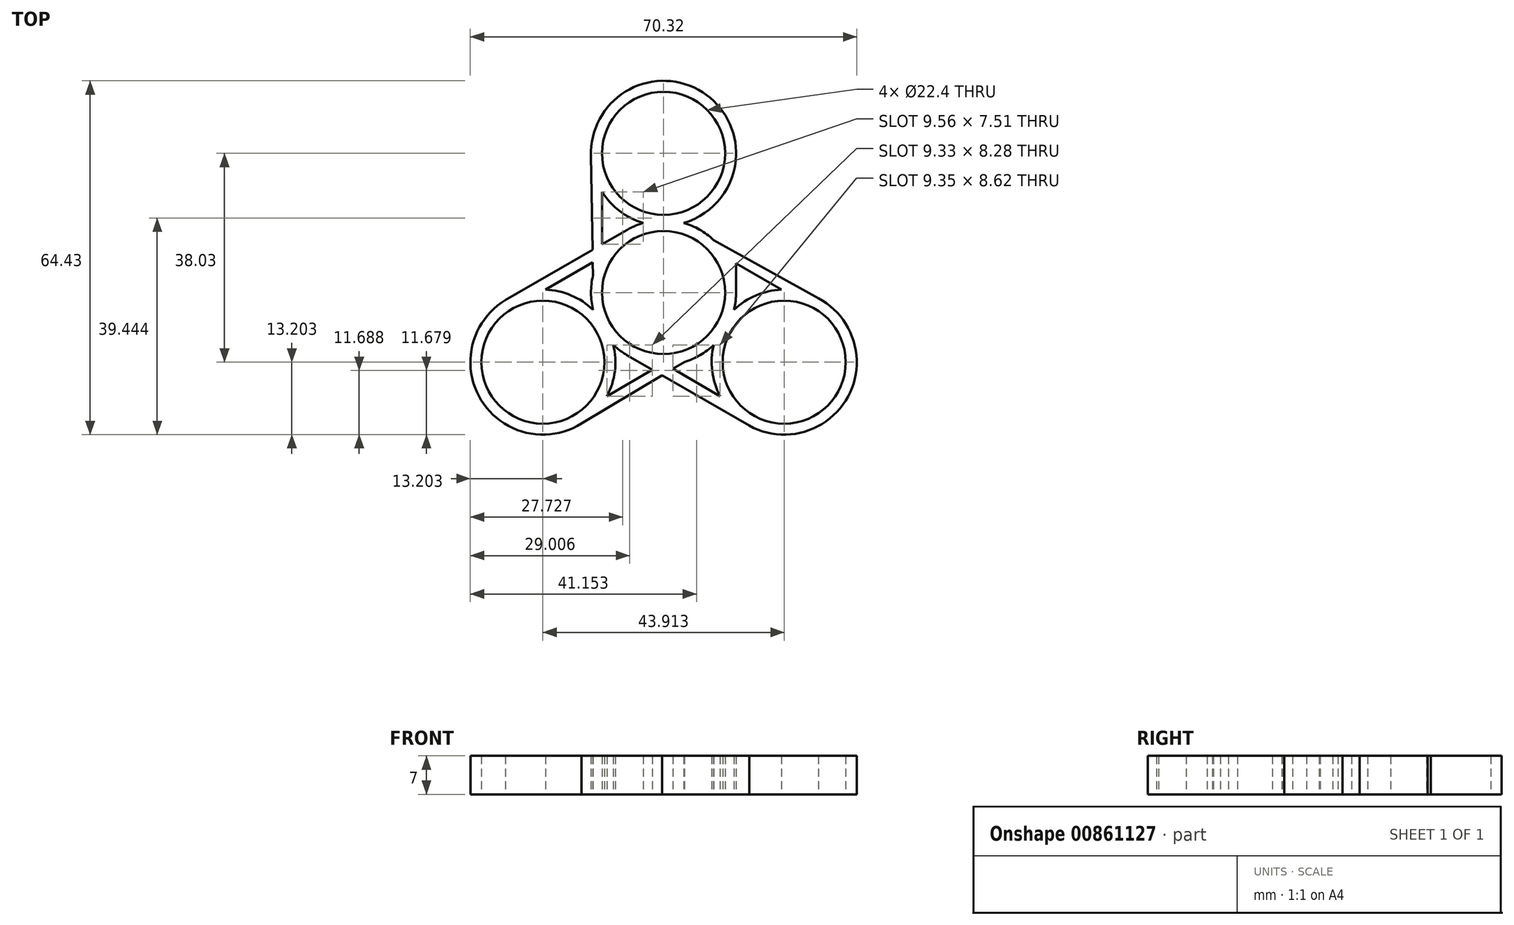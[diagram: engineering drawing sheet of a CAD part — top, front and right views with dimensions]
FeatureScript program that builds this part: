
annotation { "Feature Type Name" : "Feature", "Feature Type Description" : "" }
export const myFeature = defineFeature(function(context is Context, id is Id, definition is map)
    precondition{}
    {
        {
            var Q0;
            Q0=qCreatedBy(makeId("Top.planeOp"),FACE);
            var sketch = newSketch(context, id + "F0", { "sketchPlane" : qUnion([Q0])});
            skCircle(sketch, "E0", {"center": v(0, 0) * mm, "radius": 11.2 * mm});
            skCircle(sketch, "E1", {"center": v(0, 0) * mm, "radius": 13.2 * mm});
            skCircle(sketch, "E2", {"center": v(0, 25.35) * mm, "radius": 11.2 * mm});
            skCircle(sketch, "E3", {"center": v(0, 25.35) * mm, "radius": 13.2 * mm});
            skLineSegment(sketch, "E4", {"start": v(-11.19, 24.79) * mm, "end": v(-11.19, 7) * mm});
            skLineSegment(sketch, "E5", {"start": v(-13.2, 24.9) * mm, "end": v(-12.84, 3.06) * mm});
            skLineSegment(sketch, "E6", {"start": v(11.2, 25.06) * mm, "end": v(11.2, 7) * mm});
            skLineSegment(sketch, "E7", {"start": v(13.2, 25.62) * mm, "end": v(13.2, 0) * mm});
            skCircle(sketch, "E8.1.0", {"center": v(-21.96, -12.68) * mm, "radius": 13.2 * mm});
            skCircle(sketch, "E8.1.1", {"center": v(-21.96, -12.68) * mm, "radius": 11.2 * mm});
            skLineSegment(sketch, "E8.1.2", {"start": v(-15.87, -22.08) * mm, "end": v(-0.48, -13.2) * mm});
            skLineSegment(sketch, "E8.1.3", {"start": v(-14.96, -23.87) * mm, "end": v(3.77, -12.65) * mm});
            skLineSegment(sketch, "E8.1.4", {"start": v(-28.8, -1.38) * mm, "end": v(-6.6, 11.43) * mm});
            skLineSegment(sketch, "E8.1.5", {"start": v(-27.3, -2.83) * mm, "end": v(-11.65, 6.2) * mm});
            skCircle(sketch, "E8.2.0", {"center": v(21.96, -12.68) * mm, "radius": 13.2 * mm});
            skCircle(sketch, "E8.2.1", {"center": v(21.96, -12.68) * mm, "radius": 11.2 * mm});
            skLineSegment(sketch, "E8.2.2", {"start": v(27.06, -2.7) * mm, "end": v(11.66, 6.18) * mm});
            skLineSegment(sketch, "E8.2.3", {"start": v(28.15, -1.02) * mm, "end": v(9.07, 9.6) * mm});
            skLineSegment(sketch, "E8.2.4", {"start": v(15.6, -24.24) * mm, "end": v(-6.6, -11.43) * mm});
            skLineSegment(sketch, "E8.2.5", {"start": v(16.1, -22.22) * mm, "end": v(0.46, -13.2) * mm});
            skSolve(sketch);
        }
        {
            var Q0;
            {var subQ2=sQuery(id+"F0.wireOp",EDGE,"E4");var subQ9=sQuery(id+"F0.wireOp",EDGE,"E2");var subQ10=makeQuery(id+"F0.imprint","INTERSECT",VERTEX,{"derivedFrom":[subQ9,subQ2]});Q0=makeQuery(id+"F0.imprint","IMPRINT",FACE,{"disambiguationData":[TD([[makeQuery(id+"F0.imprint","IMPRINT",EDGE,{"disambiguationData":[TD([[subQ10,1.0]])],"derivedFrom":subQ9}),-1.0]])]});}
            var Q1;
            {var subQ0=sQuery(id+"F0.wireOp",EDGE,"E5");var subQ1=sQuery(id+"F0.wireOp",EDGE,"E3");var subQ2=makeQuery(id+"F0.imprint","INTERSECT",VERTEX,{"derivedFrom":[subQ1,subQ0]});Q1=makeQuery(id+"F0.imprint","IMPRINT",FACE,{"disambiguationData":[TD([[makeQuery(id+"F0.imprint","IMPRINT",EDGE,{"disambiguationData":[TD([[subQ2,-1.0]])],"derivedFrom":subQ1}),-1.0]])]});}
            var Q2;
            {var subQ0=sQuery(id+"F0.wireOp",EDGE,"E7");var subQ1=sQuery(id+"F0.wireOp",EDGE,"E3");var subQ2=makeQuery(id+"F0.imprint","INTERSECT",VERTEX,{"disambiguationData":[OD(1.0)],"derivedFrom":[subQ1,subQ0]});Q2=makeQuery(id+"F0.imprint","IMPRINT",FACE,{"disambiguationData":[TD([[makeQuery(id+"F0.imprint","IMPRINT",EDGE,{"disambiguationData":[TD([[subQ2,1.0]])],"derivedFrom":subQ1}),-1.0]])]});}
            var Q3;
            {var subQ0=sQuery(id+"F0.wireOp",EDGE,"E3");var subQ1=sQuery(id+"F0.wireOp",EDGE,"E1");var subQ2=makeQuery(id+"F0.imprint","INTERSECT",VERTEX,{"disambiguationData":[OD(0.0)],"derivedFrom":[subQ1,subQ0]});Q3=makeQuery(id+"F0.imprint","IMPRINT",FACE,{"disambiguationData":[TD([[makeQuery(id+"F0.imprint","IMPRINT",EDGE,{"disambiguationData":[TD([[subQ2,-1.0]])],"derivedFrom":subQ1}),1.0]])]});}
            var Q4;
            {var subQ0=sQuery(id+"F0.wireOp",EDGE,"E3");var subQ1=sQuery(id+"F0.wireOp",EDGE,"E1");var subQ2=makeQuery(id+"F0.imprint","INTERSECT",VERTEX,{"disambiguationData":[OD(0.0)],"derivedFrom":[subQ1,subQ0]});Q4=makeQuery(id+"F0.imprint","IMPRINT",FACE,{"disambiguationData":[TD([[makeQuery(id+"F0.imprint","IMPRINT",EDGE,{"disambiguationData":[TD([[subQ2,-1.0]])],"derivedFrom":subQ1}),-1.0]])]});}
            var Q5;
            {var subQ1=sQuery(id+"F0.wireOp",EDGE,"E1");var subQ7=sQuery(id+"F0.wireOp",EDGE,"E6");var subQ8=makeQuery(id+"F0.imprint","INTERSECT",VERTEX,{"derivedFrom":[subQ1,subQ7]});Q5=makeQuery(id+"F0.imprint","IMPRINT",FACE,{"disambiguationData":[TD([[makeQuery(id+"F0.imprint","IMPRINT",EDGE,{"disambiguationData":[TD([[subQ8,1.0]])],"derivedFrom":subQ1}),-1.0]])]});}
            var Q6;
            {var subQ0=sQuery(id+"F0.wireOp",EDGE,"E8.2.3");var subQ1=sQuery(id+"F0.wireOp",EDGE,"E7");var subQ2=makeQuery(id+"F0.imprint","INTERSECT",VERTEX,{"derivedFrom":[subQ1,subQ0]});Q6=makeQuery(id+"F0.imprint","IMPRINT",FACE,{"disambiguationData":[TD([[makeQuery(id+"F0.imprint","IMPRINT",EDGE,{"disambiguationData":[TD([[subQ2,-1.0]])],"derivedFrom":subQ1}),1.0]])]});}
            var Q7;
            {var subQ0=sQuery(id+"F0.wireOp",EDGE,"E7");var subQ1=sQuery(id+"F0.wireOp",EDGE,"E1");var subQ2=makeQuery(id+"F0.imprint","INTERSECT",VERTEX,{"derivedFrom":[subQ1,subQ0]});Q7=makeQuery(id+"F0.imprint","IMPRINT",FACE,{"disambiguationData":[TD([[makeQuery(id+"F0.imprint","IMPRINT",EDGE,{"disambiguationData":[TD([[subQ2,-1.0]])],"derivedFrom":subQ1}),-1.0]])]});}
            var Q8;
            {var subQ0=sQuery(id+"F0.wireOp",EDGE,"E4");var subQ1=sQuery(id+"F0.wireOp",EDGE,"E1");var subQ2=makeQuery(id+"F0.imprint","INTERSECT",VERTEX,{"derivedFrom":[subQ1,subQ0]});Q8=makeQuery(id+"F0.imprint","IMPRINT",FACE,{"disambiguationData":[TD([[makeQuery(id+"F0.imprint","IMPRINT",EDGE,{"disambiguationData":[TD([[subQ2,1.0]])],"derivedFrom":subQ1}),-1.0]])]});}
            var Q9;
            {var subQ3=sQuery(id+"F0.wireOp",EDGE,"E4");var subQ5=sQuery(id+"F0.wireOp",EDGE,"E1");var subQ6=makeQuery(id+"F0.imprint","INTERSECT",VERTEX,{"derivedFrom":[subQ5,subQ3]});Q9=makeQuery(id+"F0.imprint","IMPRINT",FACE,{"disambiguationData":[TD([[makeQuery(id+"F0.imprint","IMPRINT",EDGE,{"disambiguationData":[TD([[subQ6,-1.0]])],"derivedFrom":subQ5}),-1.0]])]});}
            var Q10;
            {var subQ0=sQuery(id+"F0.wireOp",EDGE,"E8.1.4");var subQ1=sQuery(id+"F0.wireOp",EDGE,"E5");var subQ2=makeQuery(id+"F0.imprint","INTERSECT",VERTEX,{"derivedFrom":[subQ1,subQ0]});Q10=makeQuery(id+"F0.imprint","IMPRINT",FACE,{"disambiguationData":[TD([[makeQuery(id+"F0.imprint","IMPRINT",EDGE,{"disambiguationData":[TD([[subQ2,-1.0]])],"derivedFrom":subQ1}),-1.0]])]});}
            var Q11;
            {var subQ5=sQuery(id+"F0.wireOp",EDGE,"E8.1.0");var subQ7=makeQuery(id+"F0.imprint","INTERSECT",VERTEX,{"derivedFrom":[subQ5,sQuery(id+"F0.wireOp",EDGE,"E8.1.3")]});Q11=makeQuery(id+"F0.imprint","IMPRINT",FACE,{"disambiguationData":[TD([[makeQuery(id+"F0.imprint","IMPRINT",EDGE,{"disambiguationData":[TD([[subQ7,1.0]])],"derivedFrom":subQ5}),1.0]])]});}
            var Q12;
            {var subQ5=sQuery(id+"F0.wireOp",EDGE,"E8.1.0");var subQ6=sQuery(id+"F0.wireOp",EDGE,"E1");var subQ9=makeQuery(id+"F0.imprint","INTERSECT",VERTEX,{"disambiguationData":[OD(0.0)],"derivedFrom":[subQ6,subQ5]});Q12=makeQuery(id+"F0.imprint","IMPRINT",FACE,{"disambiguationData":[TD([[makeQuery(id+"F0.imprint","IMPRINT",EDGE,{"disambiguationData":[TD([[subQ9,-1.0]])],"derivedFrom":subQ6}),-1.0]])]});}
            var Q13;
            {var subQ0=sQuery(id+"F0.wireOp",EDGE,"E8.1.2");var subQ1=sQuery(id+"F0.wireOp",EDGE,"E1");var subQ2=makeQuery(id+"F0.imprint","INTERSECT",VERTEX,{"derivedFrom":[subQ1,subQ0]});Q13=makeQuery(id+"F0.imprint","IMPRINT",FACE,{"disambiguationData":[TD([[makeQuery(id+"F0.imprint","IMPRINT",EDGE,{"disambiguationData":[TD([[subQ2,1.0]])],"derivedFrom":subQ1}),-1.0]])]});}
            var Q14;
            Q14=makeQuery(id+"F0.imprint","IMPRINT",FACE,{"disambiguationData":[TD([[makeQuery(id+"F0.imprint","IMPRINT",EDGE,{"derivedFrom":sQuery(id+"F0.wireOp",EDGE,"E0")}),-1.0]])]});
            var Q15;
            {var subQ5=sQuery(id+"F0.wireOp",EDGE,"E8.2.0");var subQ7=makeQuery(id+"F0.imprint","INTERSECT",VERTEX,{"derivedFrom":[subQ5,sQuery(id+"F0.wireOp",EDGE,"E8.2.3")]});Q15=makeQuery(id+"F0.imprint","IMPRINT",FACE,{"disambiguationData":[TD([[makeQuery(id+"F0.imprint","IMPRINT",EDGE,{"disambiguationData":[TD([[subQ7,1.0]])],"derivedFrom":subQ5}),1.0]])]});}
            var Q16;
            {var subQ5=sQuery(id+"F0.wireOp",EDGE,"E8.2.0");var subQ6=sQuery(id+"F0.wireOp",EDGE,"E1");var subQ9=makeQuery(id+"F0.imprint","INTERSECT",VERTEX,{"disambiguationData":[OD(0.0)],"derivedFrom":[subQ6,subQ5]});Q16=makeQuery(id+"F0.imprint","IMPRINT",FACE,{"disambiguationData":[TD([[makeQuery(id+"F0.imprint","IMPRINT",EDGE,{"disambiguationData":[TD([[subQ9,-1.0]])],"derivedFrom":subQ6}),-1.0]])]});}
            var Q17;
            {var subQ0=sQuery(id+"F0.wireOp",EDGE,"E8.1.0");var subQ1=sQuery(id+"F0.wireOp",EDGE,"E1");var subQ2=makeQuery(id+"F0.imprint","INTERSECT",VERTEX,{"disambiguationData":[OD(0.0)],"derivedFrom":[subQ1,subQ0]});Q17=makeQuery(id+"F0.imprint","IMPRINT",FACE,{"disambiguationData":[TD([[makeQuery(id+"F0.imprint","IMPRINT",EDGE,{"disambiguationData":[TD([[subQ2,-1.0]])],"derivedFrom":subQ1}),1.0]])]});}
            var Q18;
            {var subQ0=sQuery(id+"F0.wireOp",EDGE,"E8.2.0");var subQ1=sQuery(id+"F0.wireOp",EDGE,"E1");var subQ2=makeQuery(id+"F0.imprint","INTERSECT",VERTEX,{"disambiguationData":[OD(0.0)],"derivedFrom":[subQ1,subQ0]});Q18=makeQuery(id+"F0.imprint","IMPRINT",FACE,{"disambiguationData":[TD([[makeQuery(id+"F0.imprint","IMPRINT",EDGE,{"disambiguationData":[TD([[subQ2,-1.0]])],"derivedFrom":subQ1}),1.0]])]});}
            var Q19;
            {var subQ0=sQuery(id+"F0.wireOp",EDGE,"E8.2.4");var subQ1=sQuery(id+"F0.wireOp",EDGE,"E8.1.3");var subQ2=makeQuery(id+"F0.imprint","INTERSECT",VERTEX,{"derivedFrom":[subQ1,subQ0]});Q19=makeQuery(id+"F0.imprint","IMPRINT",FACE,{"disambiguationData":[TD([[makeQuery(id+"F0.imprint","IMPRINT",EDGE,{"disambiguationData":[TD([[subQ2,-1.0]])],"derivedFrom":subQ1}),-1.0]])]});}
            var Q20;
            {var subQ3=sQuery(id+"F0.wireOp",EDGE,"E8.1.2");var subQ5=sQuery(id+"F0.wireOp",EDGE,"E1");var subQ6=makeQuery(id+"F0.imprint","INTERSECT",VERTEX,{"derivedFrom":[subQ5,subQ3]});Q20=makeQuery(id+"F0.imprint","IMPRINT",FACE,{"disambiguationData":[TD([[makeQuery(id+"F0.imprint","IMPRINT",EDGE,{"disambiguationData":[TD([[subQ6,-1.0]])],"derivedFrom":subQ5}),-1.0]])]});}
            var Q21;
            {var subQ0=sQuery(id+"F0.wireOp",EDGE,"E8.1.3");var subQ1=sQuery(id+"F0.wireOp",EDGE,"E8.1.0");var subQ2=makeQuery(id+"F0.imprint","INTERSECT",VERTEX,{"derivedFrom":[subQ1,subQ0]});Q21=makeQuery(id+"F0.imprint","IMPRINT",FACE,{"disambiguationData":[TD([[makeQuery(id+"F0.imprint","IMPRINT",EDGE,{"disambiguationData":[TD([[subQ2,-1.0]])],"derivedFrom":subQ1}),-1.0]])]});}
            var Q22;
            {var subQ0=sQuery(id+"F0.wireOp",EDGE,"E5");var subQ1=sQuery(id+"F0.wireOp",EDGE,"E1");var subQ2=makeQuery(id+"F0.imprint","INTERSECT",VERTEX,{"derivedFrom":[subQ1,subQ0]});Q22=makeQuery(id+"F0.imprint","IMPRINT",FACE,{"disambiguationData":[TD([[makeQuery(id+"F0.imprint","IMPRINT",EDGE,{"disambiguationData":[TD([[subQ2,1.0]])],"derivedFrom":subQ1}),-1.0]])]});}
            var Q23;
            {var subQ0=sQuery(id+"F0.wireOp",EDGE,"E6");var subQ1=sQuery(id+"F0.wireOp",EDGE,"E1");var subQ2=makeQuery(id+"F0.imprint","INTERSECT",VERTEX,{"derivedFrom":[subQ1,subQ0]});Q23=makeQuery(id+"F0.imprint","IMPRINT",FACE,{"disambiguationData":[TD([[makeQuery(id+"F0.imprint","IMPRINT",EDGE,{"disambiguationData":[TD([[subQ2,-1.0]])],"derivedFrom":subQ1}),-1.0]])]});}
            var Q24;
            {var subQ0=sQuery(id+"F0.wireOp",EDGE,"E8.1.3");var subQ1=sQuery(id+"F0.wireOp",EDGE,"E1");var subQ2=makeQuery(id+"F0.imprint","INTERSECT",VERTEX,{"derivedFrom":[subQ1,subQ0]});Q24=makeQuery(id+"F0.imprint","IMPRINT",FACE,{"disambiguationData":[TD([[makeQuery(id+"F0.imprint","IMPRINT",EDGE,{"disambiguationData":[TD([[subQ2,1.0]])],"derivedFrom":subQ1}),-1.0]])]});}
            extrude(context, id + "F1", {"entities" : qUnion([Q0, Q1, Q2, Q3, Q4, Q5, Q6, Q7, Q8, Q9, Q10, Q11, Q12, Q13, Q14, Q15, Q16, Q17, Q18, Q19, Q20, Q21, Q22, Q23, Q24]), "depth" : 7 * mm, "offsetDistance" : 25 * mm});
        }
    });
